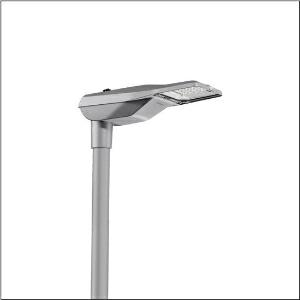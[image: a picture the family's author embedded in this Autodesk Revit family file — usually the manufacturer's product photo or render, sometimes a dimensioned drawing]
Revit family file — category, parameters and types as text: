
# Revit family: streetlight_sl_21_micro___st1_0ab_5xe1m33s08db_765d
name_source: partatom
category: Lighting Fixtures
units: mm (PartAtom-declared; Revit-internal decimal feet)

## family parameters
Cut with Voids When Loaded = No
Host = Face
Light Source = No
Part Type = Normal
Room Calculation Point = No
Round Connector Dimension = Use Diameter
Shared = No

## types (1)
- --- (1 x LED, 4500 lm, 39.1 W, 3000K)
    Apparent Load = 39 VA
    CIE Flux Codes = 38 73 97 100 100
    Color Rendering = 70
    Color Temperature = 3000K
    Default Elevation = 1800 mm
    Description = Streetlight SL 21 micro, mast luminaire, primary light control with lens, of PMMA, primary optical cover: cover, of toughened safety glass, transparent, light distribution: ST1.0aB, light emission: direct distribution, primary light characteristic: asymmetric, installation type: side-entry, post-top, LED, High Power LED, rated luminous flux: 4.500lm, luminous efficacy: 115lm/W, light colour: 730, colour temperature: 3000K, control: flexible luminous flux parameterisation, time-dependent luminous flux control, constant luminous flux control, overheat protection, presetting dimming logarithmic, mains connection: 220..240V, AC, 50/60Hz, start of lifetime: 39W, end of service life: 41W, reduction: 18W, luminaire housing, of diecast aluminium, powder-coated, Siteco® metallic grey (DB 702S), corrosivity category C5 mid according to DIN EN ISO 12944, please order mast flange separately, inclination adjustable: 0°, 5°, 10°, 15°, sealing non-destructively replaceable, multi-level sealing system, length: 528mm, width: 235mm, height: 110mm, mast flange for spigot size: 42mm (side-entry): 5XC10008XM4, 60/48mm (side-entry/post-top): 5XC10108XM2, 76/60mm (side-entry/post-top): 5XC10108XM1, Smart Interface above, protection rating (complete): IP66, insulation class (complete): insulation class II (safety insulation), certification: CE, ENEC, ENEC+, VDE, impact resistance: IK09, permissible operating ambient temperature for outdoor applications: -40..+50°C, standard-compliant lighting for roads and squares, packaging unit: 1 piece

Light Distribution: ST1.0aB
    Height = 110 mm
    Lamp = 1 x LED
    Lamp Light Flux = 4500 lm
    Lamp Power = 39.1 W
    Lamp count = 1
    Length = 528 mm
    Luminous efficacy = 115 lm/W
    Manufacturer = Siteco
    ModVariant = No
    Model = 5XE1M33S08DB
    Number of Poles = 1
    OnlyDefault = Yes
    Power Factor = 1
    Product Name = Streetlight SL 21 micro | ST1.0aB
    Product group = mast luminaire | pylon top
    ProductGroupID = 6100
    Protection Class = Protection class II
    Protection Degree = IP 66
    RLX_Detail_Level = 1
    RLX_Emergency_Light_Flux = 0 lm
    RLX_Emergency_Type = 0
    RLX_Emergency_Type_DB = No
    RlxData = <blob elided: 98765 chars, md5=04fe7f07>
    Socket = socket
    Standby Power = 0 W
    System Light Flux = 4500 lm
    System Power = 39 W
    Type Comments = factory setting: luminous flux: 100 % | dim-lin: 254 | 765 mA
    Type Image = l_1277292.jpg
    URL = http://relux.com
    VarID = @adj_104133
    Voltage = 0 V
    Weight = 0.00 kg
    Width = 235 mm

## geometry (parser evidence)
native form markers: Blend x4, Sweep x11
no freeform markers — native parametric forms only
